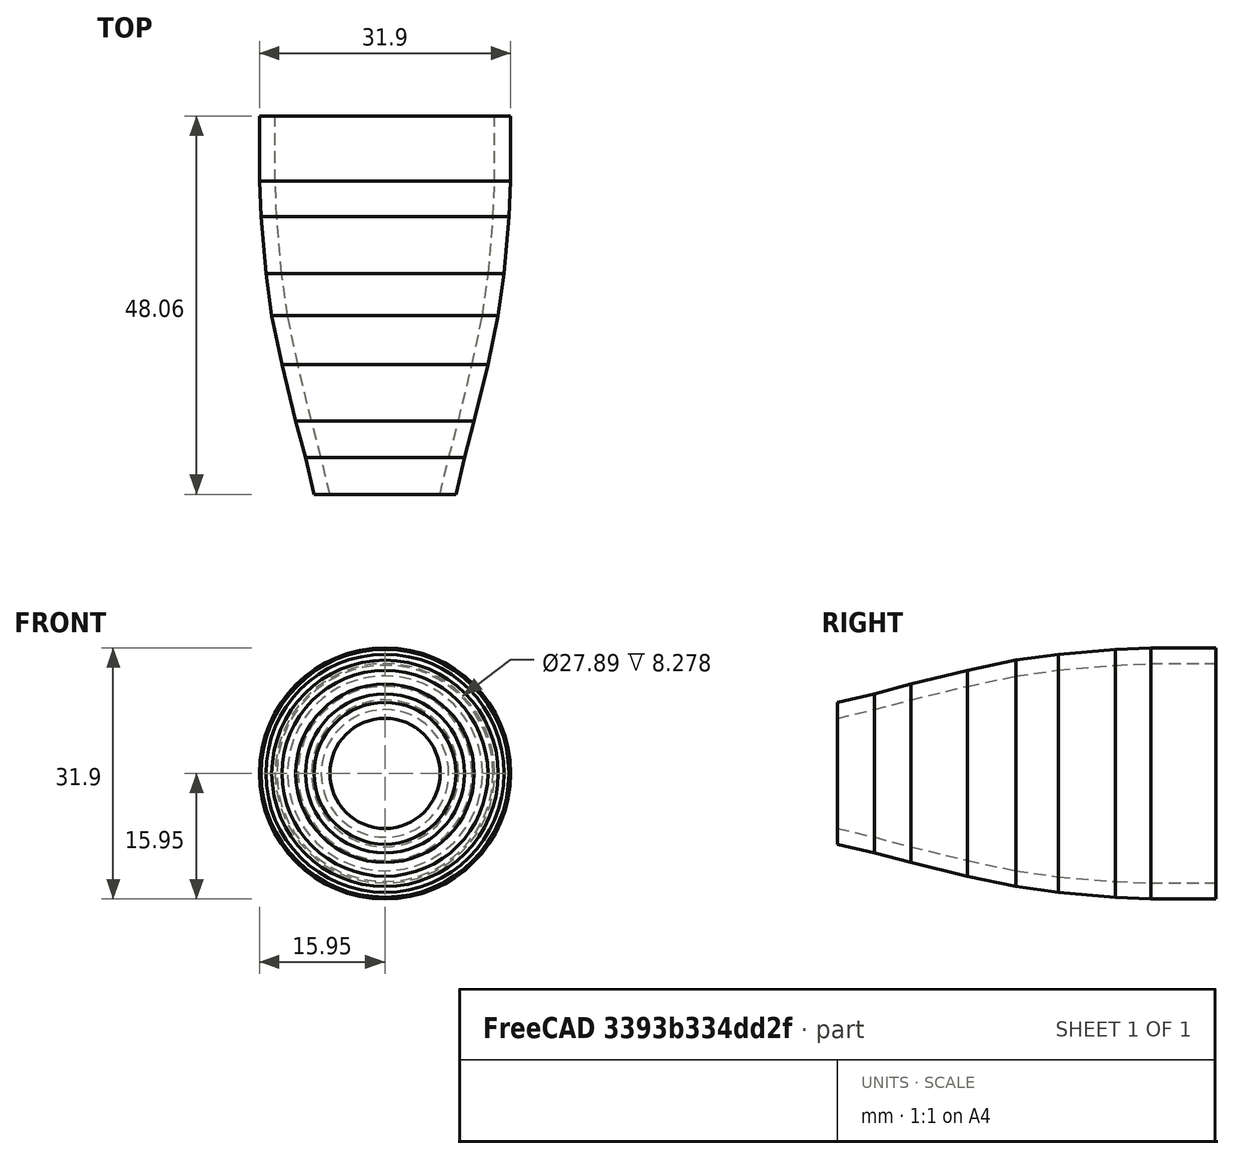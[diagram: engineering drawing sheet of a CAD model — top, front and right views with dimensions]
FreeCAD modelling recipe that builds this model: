
FCSTD DOCUMENT  (FreeCAD 0.21R33771 (Git))
Label: tejhabosito-tarto
License: All rights reserved
LicenseURL: http://en.wikipedia.org/wiki/All_rights_reserved
objects: Image::ImagePlane×1, Sketcher::SketchObject×1, PartDesign::Revolution×1, PartDesign::Body×1, Spreadsheet::Sheet×1
note: 4 computed .brp shape members not serialized (recipe doc carries the construction recipe); baked Part::Feature solids carry a one-line shape summary decoded from their .brp

FEATURE [Image::ImagePlane] IMG_20240105_192248
  Placement = pos=(9,28,0) rot=(0,0,1;1.5708rad)
  XSize = 100.827
  YSize = 75.62
FEATURE [Sketcher::SketchObject] Sketch
  FullyConstrained = true
  expr: Constraints[16] = <<Parameters>>.tip_diameter / 2
  expr: Constraints[20] = <<Parameters>>.wall_thickness
  expr: Constraints[39] = <<Parameters>>.wall_thickness
  expr: Constraints[41] = <<Parameters>>.wall_thickness
  sketch-geometry (18):
    g0: LineSegment StartX=7 StartY=0 StartZ=0 EndX=8.09979 EndY=4.70299 EndZ=0
    g1: LineSegment StartX=8.09979 StartY=4.70299 StartZ=0 EndX=9.32964 EndY=9.30206 EndZ=0
    g2: LineSegment StartX=9.32964 StartY=9.30206 StartZ=0 EndX=11.0665 EndY=16.505 EndZ=0
    g3: LineSegment StartX=11.0665 StartY=16.505 StartZ=0 EndX=12.377 EndY=22.6833 EndZ=0
    g4: LineSegment StartX=12.377 StartY=22.6833 StartZ=0 EndX=13.1259 EndY=28.0503 EndZ=0
    g5: LineSegment StartX=13.1259 StartY=28.0503 StartZ=0 EndX=13.7385 EndY=35.3054 EndZ=0
    g6: LineSegment StartX=13.7385 StartY=35.3054 StartZ=0 EndX=13.945 EndY=39.781 EndZ=0
    g7: LineSegment StartX=13.945 StartY=39.781 StartZ=0 EndX=13.945 EndY=48.0594 EndZ=0
    g8: LineSegment StartX=15.945 StartY=48.0594 StartZ=0 EndX=15.945 EndY=39.781 EndZ=0
    g9: LineSegment StartX=15.945 StartY=39.781 StartZ=0 EndX=15.7385 EndY=35.3054 EndZ=0
    g10: LineSegment StartX=15.1259 StartY=28.0503 StartZ=0 EndX=14.377 EndY=22.6833 EndZ=0
    g11: LineSegment StartX=14.377 StartY=22.6833 StartZ=0 EndX=13.0665 EndY=16.505 EndZ=0
    g12: LineSegment StartX=13.0665 StartY=16.505 StartZ=0 EndX=11.3296 EndY=9.30206 EndZ=0
    g13: LineSegment StartX=11.3296 StartY=9.30206 StartZ=0 EndX=10.0998 EndY=4.70299 EndZ=0
    g14: LineSegment StartX=10.0998 StartY=4.70299 StartZ=0 EndX=9 EndY=0 EndZ=0
    g15: LineSegment StartX=9 StartY=0 StartZ=0 EndX=7 EndY=0 EndZ=0
    g16: LineSegment StartX=13.945 StartY=48.0594 StartZ=0 EndX=15.945 EndY=48.0594 EndZ=0
    g17: LineSegment StartX=15.7385 StartY=35.3054 StartZ=0 EndX=15.1259 EndY=28.0503 EndZ=0
  constraints (54):
    c: PointOnObject(g0,g-1)
    c: Coincident(g0,g1)
    c: Coincident(g1,g2)
    c: Coincident(g2,g3)
    c: Coincident(g3,g4)
    c: Coincident(g4,g5)
    c: Coincident(g5,g6)
    c: Coincident(g6,g7)
    c: Vertical(g7)
    c: Vertical(g8)
    c: Coincident(g8,g9)
    c: Coincident(g10,g11)
    c: Coincident(g11,g12)
    c: Coincident(g12,g13)
    c: Coincident(g13,g14)
    c: Horizontal(g6,g8)
    c: DistanceX(g-1,g0) = 7
    c: Coincident(g15,g14)
    c: Coincident(g15,g0)
    c: Horizontal(g15)
    c: DistanceX(g15,g15) = 2
    c: DistanceX(g0) = 8.09979
    c: DistanceY(g0) = 4.70299
    c: DistanceX(g1) = 9.32964
    c: DistanceY(g1) = 9.30206
    c: DistanceX(g2) = 11.0665
    c: DistanceY(g2) = 16.505
    c: DistanceX(g3) = 12.377
    c: DistanceY(g3) = 22.6833
    c: DistanceX(g4) = 13.1259
    c: DistanceY(g4) = 28.0503
    c: DistanceX(g5) = 13.7385
    c: DistanceY(g5) = 35.3054
    c: DistanceX(g6) = 13.945
    c: DistanceY(g6) = 39.781
    c: Coincident(g16,g7)
    c: Coincident(g16,g8)
    c: Horizontal(g16)
    c: DistanceY(g7) = 48.0594
    c: DistanceX(g16,g16) = 2
    c: Horizontal(g5,g9)
    c: DistanceX(g5,g9) = 2
    c: Horizontal(g4,g10)
    c: DistanceX(g4,g10) = 2
    c: Coincident(g17,g9)
    c: Coincident(g17,g10)
    c: Horizontal(g3,g10)
    c: DistanceX(g3,g10) = 2
    c: Horizontal(g2,g11)
    c: DistanceX(g2,g11) = 2
    c: Horizontal(g1,g12)
    c: DistanceX(g1,g12) = 2
    c: Horizontal(g0,g13)
    c: DistanceX(g0,g13) = 2
FEATURE [PartDesign::Revolution] Revolution
  Angle = 360
  Axis = (0,1,0)
  Base = (0,0,0)
  Profile = -> Sketch
  ReferenceAxis = -> Sketch [V_Axis]
  Reversed = true
FEATURE [PartDesign::Body] Body
  Group = -> [Sketch,Revolution]
  Origin = -> Origin
  Tip = -> Revolution
FEATURE [Spreadsheet::Sheet] Spreadsheet  label="Parameters"
  cells = A1='wall_thickness; B1(wall_thickness)=2; A2='tip_diameter; B2(tip_diameter)=14; A3='max_diameter; B3(max_diameter)=30; A4='holder_height; B4(holder_height)=100; A5='attachment_diameter; B5(attachment_diameter)=2; A6='attachment_height; B6(attachment_height)=100
